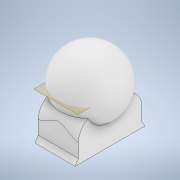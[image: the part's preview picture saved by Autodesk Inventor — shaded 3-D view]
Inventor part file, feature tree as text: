
AUTODESK INVENTOR PART (.ipt)
format: ipt  version: 2021.3 (Build 253353000, 353)  size: 258,560 bytes
history: native  units: mm
features: sketch x5, plane x2, extrude x2, loft x1, revolve x1, fillet x1
ambient origin geometry x8: Origin, YZ Plane, XZ Plane, XY Plane, X Axis, Y Axis, Z Axis, Center Point
bodies: Solid1 (feature_tree)
feature tree (12):
  sketch  "Sketch1"  dims[d0=19.0mm d1=33.0mm]
  plane  "Work Plane1"
  sketch  "Sketch3"  dims[d26=2.5mm d27=0.0mm d28=0.0mm]
  loft  "base"
  extrude  "Extrusion8"  TaperAngle=0.0deg  [1 undecoded]
  extrude  "brass_insert_holes"  Depth=30.0mm
  plane  "Work Plane2"
  revolve  "Revolution1"  Angle=90.0deg
  fillet  "Fillet4"  [1 undecoded]
  sketch  "Sketch14"  dims[d31=1.5mm]
  sketch  "Sketch15"  dims[d32=19.0mm d33=33.0mm d34=3.0mm d35=3.0mm d36=3.0mm d37=3.0mm d38=3.0mm d39=3.0mm d40=3.5mm d41=3.5mm d42=16.5mm d43=16.5mm d44=7.5mm d45=7.5mm d46=7.5mm d47=7.5mm d48=6.5mm d49=6.5mm d50=6.5mm d51=6.5mm d52=0.0mm d53=0.0mm d54=0.0mm d55=90.0deg d56=0.0mm d57=90.0deg d58=20.0mm d59=0.0mm d106=12.0mm d116=14.0mm d117=0.0mm d118=5.0mm d119=360.0deg d120=8.0mm d66=0.5mm d67=0.872665mm d68=0.5mm d69=0.872665mm]
  sketch  "Sketch4"  dims[d29=19.0mm d30=30.0mm]
note: 2 required parameter values undecoded (feature->parameter linkage not recoverable at this tier; creation-order binding heuristic only, values carry confidence <= 0.55)
